# Revit family: Camera-Security-Panasonic-360-degree-Vandal_Resistant-Outdoor-Dome-Network-SFV481X
name_source: partatom
category: Security Devices
revit_build: Autodesk Revit 2013 (Build: 20130531_2115(x64)
units: mm (PartAtom-declared; Revit-internal decimal feet)

## types (1)
- WV-SFV481
    Alarm Input Or Output Specification = ALARM IN1 (DAY/NIGHT IN), ALARM IN2 (ALARM OUT), ALARM IN3 (AUX OUT)
    Angle Of View = 180
    Audio In = Yes
    Audio Out = Yes
    Communication Ports = 10Base-T / 100Base-TX, RJ-45
    Date Last Modified = December, 13, 2016
    Day Or Night = Yes
    Default Elevation = 0 "
    Description = Security Camera, 360-degree, Vandal Resistant, Outdoor, Dome, 9 Megapixel, Network, SFV481
    Equipment Abbreviation = SC
    Family Version = 1.0.0
    Focal Length = 0.054 "
    Has POE = Yes
    IP Or Analog = IP
    Indoor Or Outdoor = Outdoor
    Manufacturer = Panasonic
    Minimum Illumination = 0 lx
    Model = WV-SFV481
    Model Disclaimer = Contact Panasonic for more information
    Mounting Positions = Mount Dependent or Surface Mount
    Operational Humidity = 10% to 90% (no condensation)
    Operational Temperature = -40°F - 122°F
    PPM Target Height = 70.079 "
    Part Description = Security Camera, 360-degree, Vandal Resistant, Outdoor, Dome, 9 Megapixel, Network, SFV481
    Part Number = WV-SFV481
    Power Active = 10.9 W
    Product Documentation Link = http://ssbu-t.psn-web.net
    Product Material = Paint - Panasonic - Sail White
    Product Page URL = http://security.panasonic.com
    Provide Feedback = https://www.surveymonkey.com
    Regulatory Compliance = UL UL60950-1, C-UL CAN/CSA C22.2 No.60950-1, CE, IEC60950-1 FCC Part15 ClassA, ICES003 ClassA, EN55022 ClassB, EN55024
    Scanning Area H = 0.218 "
    Scanning Area V = 0.218 "
    Shock Resistance = Compliant with 50J (IEC 60068-2-75 / IK10 (IEC 62262)
    Storage Temperature = -40°F - 149°F
    URL = http://security.panasonic.com
    Vandal Resistant = Yes
    Voltage AC = 12 V
    Water and Dust Resistance = IP66, IEC60529 measuring standard compatible, Type 4X(UL50), NEMA 4X compliant
    Wide Dynamic Range = Yes
    z Horizontal FOV = 180.00°
    z Vertical FOV = 180.00°

## geometry (parser evidence)
native form markers: Sweep x2
no freeform markers — native parametric forms only
